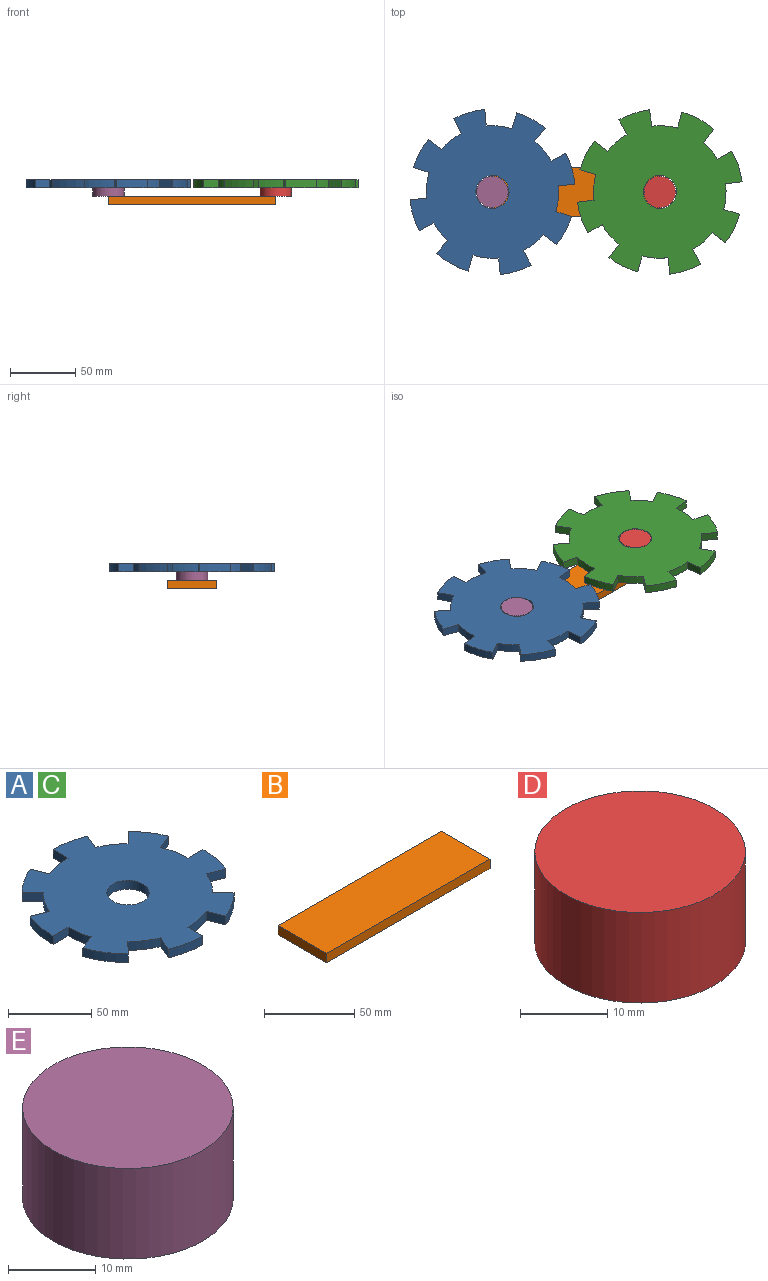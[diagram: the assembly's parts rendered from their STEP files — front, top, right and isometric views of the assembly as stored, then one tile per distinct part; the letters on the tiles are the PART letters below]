
ASSEMBLY  parts=5 mates=4
PART A: 35 faces, bbox 127x127x6.4 mm
  f0: plane 11.73x6.35mm, normal (-0.38,-0.92,0), area 80.6mm2, adj f1,f32,f33,f34
  f1: cylinder r=63.5mm len=24.3mm, axis (0,0,-1), area 158.3mm2, adj f0,f2,f33,f34
  f2: plane 12.7x6.35mm, normal (0,1,0), area 80.6mm2, adj f1,f3,f33,f34
  f3: cylinder r=50.8mm len=19.44mm, axis (0,0,-1), area 126.7mm2, adj f2,f4,f33,f34
  f4: plane 11.73x6.35mm, normal (0.38,-0.92,0), area 80.6mm2, adj f3,f5,f33,f34
  f5: cylinder r=63.5mm len=20.6mm, axis (0,0,-1), area 158.3mm2, adj f4,f6,f33,f34
  f6: plane 8.98x8.98mm, normal (-0.71,0.71,0), area 80.6mm2, adj f5,f7,f33,f34
  f7: cylinder r=50.8mm len=16.48mm, axis (0,0,-1), area 126.7mm2, adj f6,f8,f33,f34
  f8: plane 11.73x6.35mm, normal (0.92,-0.38,0), area 80.6mm2, adj f7,f9,f33,f34
  f9: cylinder r=63.5mm len=24.3mm, axis (0,0,-1), area 158.3mm2, adj f8,f10,f33,f34
  f10: plane 12.7x6.35mm, normal (-1,0,0), area 80.6mm2, adj f9,f11,f33,f34
  f11: cylinder r=50.8mm len=19.44mm, axis (0,0,-1), area 126.7mm2, adj f10,f12,f33,f34
  f12: plane 11.73x6.35mm, normal (0.92,0.38,0), area 80.6mm2, adj f11,f13,f33,f34
  f13: cylinder r=63.5mm len=20.6mm, axis (0,0,-1), area 158.3mm2, adj f12,f14,f33,f34
  f14: plane 8.98x8.98mm, normal (-0.71,-0.71,0), area 80.6mm2, adj f13,f15,f33,f34
  f15: cylinder r=50.8mm len=16.48mm, axis (0,0,-1), area 126.7mm2, adj f14,f16,f33,f34
  f16: plane 11.73x6.35mm, normal (0.38,0.92,0), area 80.6mm2, adj f15,f17,f33,f34
  f17: cylinder r=63.5mm len=24.3mm, axis (0,0,-1), area 158.3mm2, adj f16,f18,f33,f34
  f18: plane 12.7x6.35mm, normal (0,-1,0), area 80.6mm2, adj f17,f19,f33,f34
  f19: cylinder r=50.8mm len=16.71mm, axis (0,0,-1), area 108.1mm2, adj f18,f20,f33,f34
  f20: plane 11.75x6.35mm, normal (-0.38,0.92,0), area 80.8mm2, adj f19,f21,f33,f34
  f21: cylinder r=63.5mm len=23.33mm, axis (0,0,-1), area 176.9mm2, adj f20,f22,f33,f34
  f22: plane 8.98x8.98mm, normal (0.71,-0.71,0), area 80.6mm2, adj f21,f23,f33,f34
  f23: cylinder r=50.8mm len=16.48mm, axis (0,0,-1), area 126.7mm2, adj f22,f24,f33,f34
  f24: plane 11.73x6.35mm, normal (-0.92,0.38,0), area 80.6mm2, adj f23,f25,f33,f34
  f25: cylinder r=63.5mm len=24.3mm, axis (0,0,-1), area 158.3mm2, adj f24,f26,f33,f34
  f26: plane 12.7x6.35mm, normal (1,0,0), area 80.6mm2, adj f25,f27,f33,f34
  f27: cylinder r=50.8mm len=19.44mm, axis (0,0,-1), area 126.7mm2, adj f26,f28,f33,f34
  f28: plane 11.73x6.35mm, normal (-0.92,-0.38,0), area 80.6mm2, adj f27,f29,f33,f34
  f29: cylinder r=63.5mm len=20.6mm, axis (0,0,-1), area 158.3mm2, adj f28,f30,f33,f34
  f30: plane 8.98x8.98mm, normal (0.71,0.71,0), area 80.6mm2, adj f29,f32,f33,f34
  f31: cylinder r=12.7mm len=25.4mm, axis (0,0,-1), area 506.7mm2, adj f33,f34
  f32: cylinder r=50.8mm len=16.48mm, axis (0,0,-1), area 126.7mm2, adj f0,f30,f33,f34
  f33: plane 127x127mm, normal (0,0,1), area 9917.9mm2, adj f0,f1,f2,f3,f4,f5,f6,f7
  f34: plane 127x127mm, normal (0,0,-1), area 9917.9mm2, adj f0,f1,f2,f3,f4,f5,f6,f7
PART B: 6 faces, bbox 128.3x38.1x6.4 mm
  f0: plane 128.27x6.35mm, normal (0,-1,0), area 814.5mm2, adj f1,f3,f4,f5
  f1: plane 38.1x6.35mm, normal (1,0,0), area 241.9mm2, adj f0,f2,f4,f5
  f2: plane 128.27x6.35mm, normal (0,1,0), area 814.5mm2, adj f1,f3,f4,f5
  f3: plane 38.1x6.35mm, normal (-1,0,0), area 241.9mm2, adj f0,f2,f4,f5
  f4: plane 128.27x38.1mm, normal (0,0,1), area 4887.1mm2, adj f0,f1,f2,f3
  f5: plane 128.27x38.1mm, normal (0,0,-1), area 4887.1mm2, adj f0,f1,f2,f3
PART C: same geometry as A
PART D: 3 faces, bbox 24.1x24.1x12.7 mm
  f0: cylinder r=12.06mm len=24.13mm, axis (0,0,-1), area 962.7mm2, adj f1,f2
  f1: plane 24.13x24.13mm, normal (0,0,1), area 457.3mm2, adj f0
  f2: plane 24.13x24.13mm, normal (0,0,-1), area 457.3mm2, adj f0
PART E: 3 faces, bbox 24.1x24.1x12.7 mm
  f0: cylinder r=12.06mm len=24.13mm, axis (0,0,-1), area 962.7mm2, adj f1,f2
  f1: plane 24.13x24.13mm, normal (0,0,1), area 457.3mm2, adj f0
  f2: plane 24.13x24.13mm, normal (0,0,-1), area 457.3mm2, adj f0
PLACE A rot(axis=(0,0,1),27.9deg) t=(-60.96,2.65,13.93)mm
PLACE B t=(3.18,2.65,1.23)mm fixed
PLACE C rot(axis=(0,0,-1),150.4deg) t=(67.31,2.65,13.93)mm
PLACE D t=(15.88,2.65,1.23)mm
PLACE E t=(-9.52,2.65,1.23)mm
MATE fastened B.f4 <-> E.f0  axis (0,0,1) through (-60.96,2.65,7.58)mm
MATE revolute A.f1 <-> E.f0  axis (0,0,1) through (-60.96,2.65,20.28)mm
MATE fastened B.f4 <-> D.f0  axis (0,0,1) through (67.31,2.65,7.58)mm
MATE revolute C.f1 <-> D.f0  axis (0,0,1) through (67.31,2.65,20.28)mm
